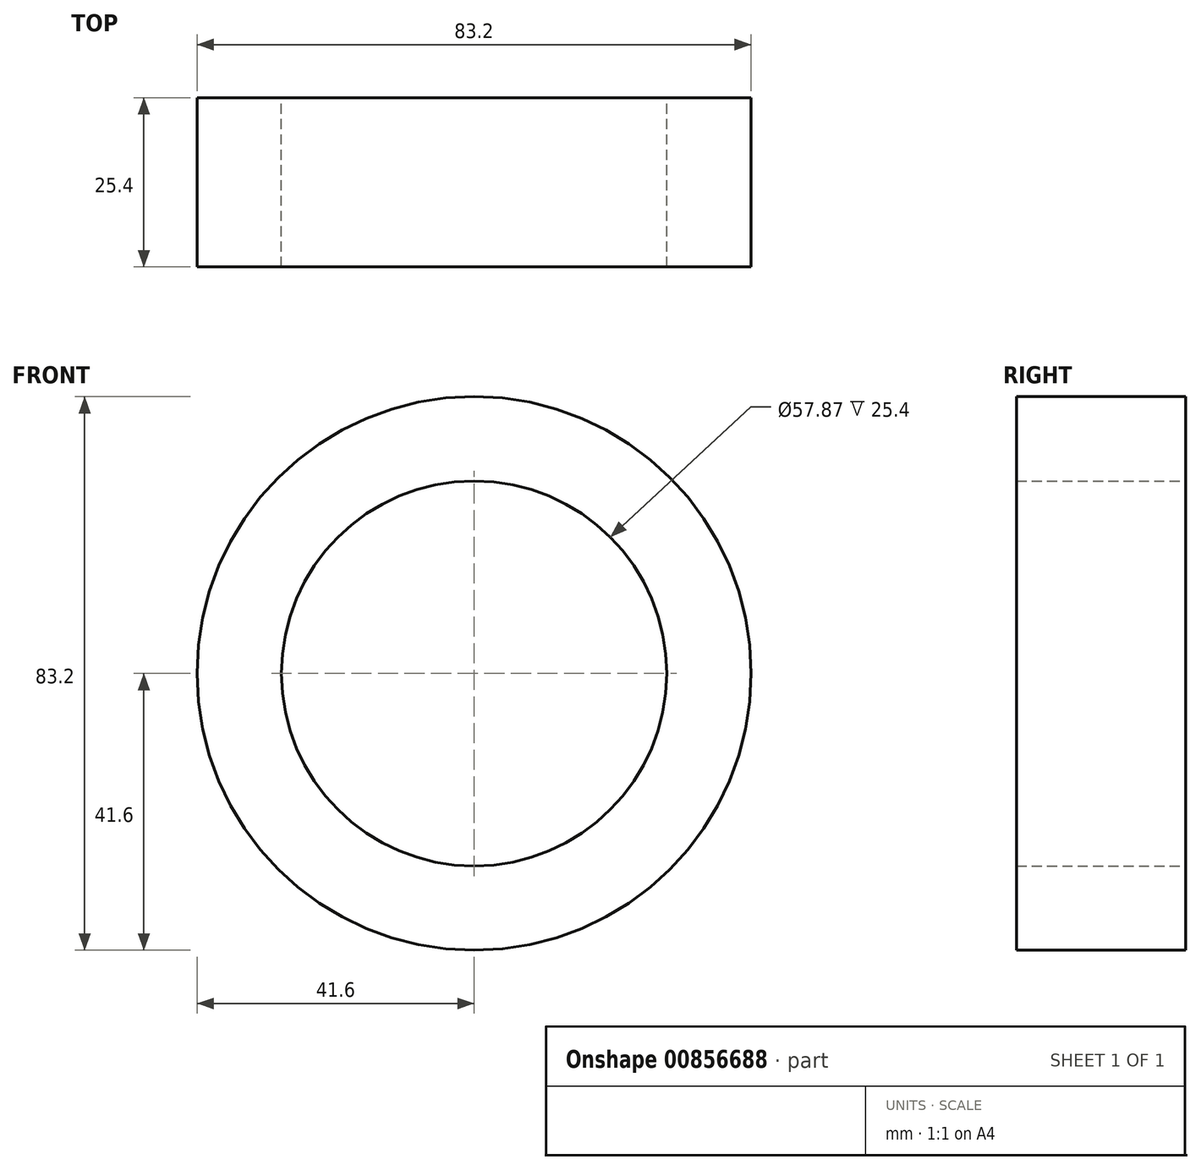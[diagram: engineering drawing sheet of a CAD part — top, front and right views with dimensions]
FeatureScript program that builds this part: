
annotation { "Feature Type Name" : "Feature", "Feature Type Description" : "" }
export const myFeature = defineFeature(function(context is Context, id is Id, definition is map)
    precondition{}
    {
        {
            var Q0;
            Q0=qCreatedBy(makeId("Front.planeOp"),FACE);
            var sketch = newSketch(context, id + "F0", { "sketchPlane" : qUnion([Q0])});
            skCircle(sketch, "E0", {"center": v(0, 0) * mm, "radius": 41.6 * mm});
            skCircle(sketch, "E1", {"center": v(0, 0) * mm, "radius": 28.94 * mm});
            skSolve(sketch);
        }
        {
            var Q0;
            Q0=makeQuery(id+"F0.imprint","IMPRINT",FACE,{"disambiguationData":[TD([[makeQuery(id+"F0.imprint","IMPRINT",EDGE,{"derivedFrom":sQuery(id+"F0.wireOp",EDGE,"E0")}),1.0]])]});
            extrude(context, id + "F1", {"entities" : qUnion([Q0]), "depth" : 25.4 * mm, "offsetDistance" : 25.4 * mm});
        }
    });
